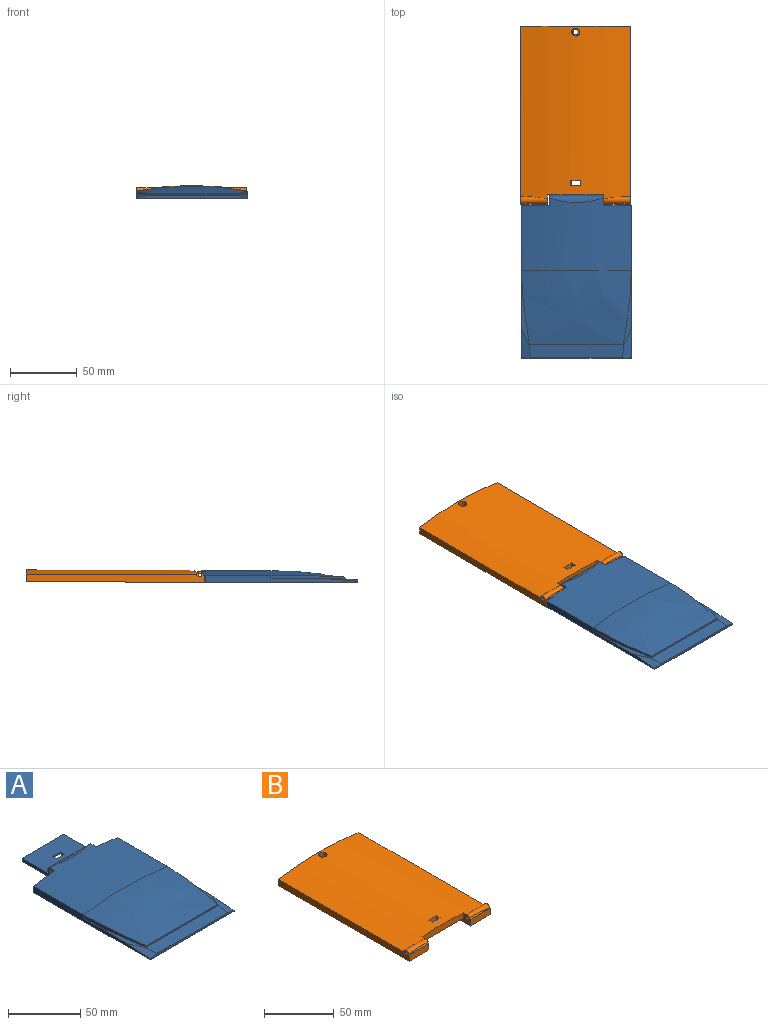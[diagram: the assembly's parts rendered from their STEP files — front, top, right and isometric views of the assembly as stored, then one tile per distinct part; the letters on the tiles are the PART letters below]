
ASSEMBLY  parts=2 mates=1
PART A: 33 faces, bbox 82x146x8.9 mm
  f0: plane 146x82mm, normal (0,0,-1), area 10463.6mm2, adj f2,f3,f7,f15,f16,f17,f18,f23
  f1: plane 40.8x2.7mm, normal (0,1,0), area 110.2mm2, adj f17,f18,f21,f22
  f2: plane 114x5.5mm, normal (1,0,0), area 419mm2, adj f0,f5,f6,f7,f9,f11,f15
  f3: plane 114x5.5mm, normal (-1,0,0), area 419mm2, adj f0,f4,f5,f7,f8,f13,f16
  f4: plane 55x6mm, normal (0,0,1), area 91mm2, adj f3,f8,f13,f14
  f5: cylinder r=250mm len=82mm, axis (0,1,0), area 4170mm2, adj f2,f3,f12,f15,f16,f17,f18,f20
  f6: plane 55x6mm, normal (0,0,1), area 91mm2, adj f2,f9,f11,f14
  f7: plane 82x2mm, normal (0,-1,0), area 156.3mm2, adj f0,f2,f3,f8,f9,f14
  f8: plane 22x6.61mm, normal (-0.17,-0.08,0.98), area 94.8mm2, adj f3,f4,f7,f14
  f9: plane 22x6.61mm, normal (0.17,-0.08,0.98), area 94.8mm2, adj f2,f6,f7,f14
  f10: plane 70x1.4mm, normal (0,-1,0), area 98mm2, adj f11,f12,f13,f14
  f11: bspline ~55x6mm, area 129.4mm2, adj f2,f6,f10,f12
  f12: bspline ~82x55mm, area 4285.9mm2, adj f5,f10,f11,f13
  f13: bspline ~55x6mm, area 129.4mm2, adj f3,f4,f10,f12
  f14: plane 71.09x10mm, normal (0,-0.06,1), area 700.6mm2, adj f4,f6,f7,f8,f9,f10
  f15: plane 20.6x8.05mm, normal (0,1,0), area 142.6mm2, adj f0,f2,f5,f17
  f16: plane 20.6x8.05mm, normal (0,1,0), area 142.6mm2, adj f0,f3,f5,f18
  f17: plane 32x8.05mm, normal (1,0,0), area 117.7mm2, adj f0,f1,f5,f15,f19,f21,f22,f23
  f18: plane 32x8.05mm, normal (-1,0,0), area 117.7mm2, adj f0,f1,f5,f16,f19,f21,f22,f23
  f19: cylinder r=1.25mm len=40.8mm, axis (1,0,0), area 320.4mm2, adj f17,f18
  f20: plane 33.11x2.62mm, normal (0,0.21,0.98), area 59mm2, adj f5,f21
  f21: cylinder r=3mm len=40.8mm, axis (1,0,0), area 163.7mm2, adj f1,f5,f17,f18,f20
  f22: plane 40.8x25mm, normal (0,0,1), area 988mm2, adj f1,f17,f18,f23,f29,f30,f31,f32
  f23: plane 40.8x2.7mm, normal (0,1,0), area 110.2mm2, adj f0,f17,f18,f22
  f24: plane 19x1.3mm, normal (0,-1,0), area 24.7mm2, adj f0,f25,f27,f28
  f25: plane 10x1.3mm, normal (-1,0,0), area 13mm2, adj f0,f24,f26,f28
  f26: plane 19x1.3mm, normal (0,1,0), area 24.7mm2, adj f0,f25,f27,f28
  f27: plane 10x1.3mm, normal (1,0,0), area 13mm2, adj f0,f24,f26,f28
  f28: plane 19x10mm, normal (0,0,-1), area 158mm2, adj f24,f25,f26,f27,f29,f30,f31,f32
  f29: plane 4x1.4mm, normal (-1,0,0), area 5.6mm2, adj f22,f28,f30,f32
  f30: plane 8x1.4mm, normal (0,1,0), area 11.2mm2, adj f22,f28,f29,f31
  f31: plane 4x1.4mm, normal (1,0,0), area 5.6mm2, adj f22,f28,f30,f32
  f32: plane 8x1.4mm, normal (0,-1,0), area 11.2mm2, adj f22,f28,f29,f31
PART B: 27 faces, bbox 82x133x8.9 mm
  f0: cylinder r=250mm len=8.18mm, axis (0,1,0), area 1.1mm2, adj f10,f12,f20
  f1: plane 33x8.05mm, normal (-1,0,0), area 140mm2, adj f7,f8,f11,f13,f16,f17,f19,f21
  f2: plane 6x6mm, normal (0,0,1), area 15.7mm2, adj f3,f5
  f3: cylinder r=3mm len=7.47mm, axis (0,0,-1), area 140.7mm2, adj f2,f11
  f4: plane 82x8.89mm, normal (0,1,0), area 636.3mm2, adj f7,f11,f12,f14
  f5: cylinder r=2mm len=4mm, axis (0,0,-1), area 17.6mm2, adj f2,f7
  f6: cylinder r=1.25mm len=20mm, axis (1,0,0), area 157.1mm2, adj f12,f15
  f7: plane 133x82mm, normal (0,0,-1), area 9507.4mm2, adj f1,f4,f5,f12,f14,f15,f17,f18
  f8: cylinder r=2.65mm len=20mm, axis (1,0,0), area 110mm2, adj f1,f9,f11,f14,f19
  f9: cylinder r=250mm len=8.18mm, axis (0,1,0), area 1.1mm2, adj f8,f14,f19
  f10: cylinder r=2.65mm len=20mm, axis (1,0,0), area 110mm2, adj f0,f11,f12,f15,f20
  f11: cylinder r=250mm len=129.49mm, axis (0,1,0), area 10399.8mm2, adj f1,f3,f4,f8,f10,f12,f14,f15
  f12: plane 133x8.05mm, normal (-1,0,0), area 737.1mm2, adj f0,f4,f6,f7,f10,f11,f18
  f13: cylinder r=1.25mm len=20mm, axis (1,0,0), area 157.1mm2, adj f1,f14
  f14: plane 133x8.05mm, normal (1,0,0), area 737.1mm2, adj f4,f7,f8,f9,f11,f13,f17
  f15: plane 33x8.05mm, normal (1,0,0), area 140mm2, adj f6,f7,f10,f11,f16,f18,f20,f21
  f16: plane 42x5.39mm, normal (0,-1,0), area 213.8mm2, adj f1,f11,f15,f21
  f17: plane 20x5.5mm, normal (0,-1,0), area 110mm2, adj f1,f7,f14,f19
  f18: plane 20x5.5mm, normal (0,-1,0), area 110mm2, adj f7,f12,f15,f20
  f19: plane 20.04x1.26mm, normal (0,-0.87,0.5), area 22.6mm2, adj f1,f8,f9,f17
  f20: plane 20.04x1.26mm, normal (0,-0.87,0.5), area 22.6mm2, adj f0,f10,f15,f18
  f21: plane 42x26mm, normal (0,0,-1), area 1060mm2, adj f1,f15,f16,f22,f23,f24,f25,f26
  f22: plane 42x3.5mm, normal (0,-1,0), area 147mm2, adj f1,f7,f15,f21
  f23: plane 5.35x4mm, normal (-1,0,0), area 21.4mm2, adj f11,f21,f24,f26
  f24: plane 8x5.39mm, normal (0,1,0), area 43mm2, adj f11,f21,f23,f25
  f25: plane 5.35x4mm, normal (1,0,0), area 21.4mm2, adj f11,f21,f24,f26
  f26: plane 8x5.39mm, normal (0,-1,0), area 43mm2, adj f11,f21,f23,f25
PLACE A t=(-101.88,43.36,-37.11)mm fixed
PLACE B rot(axis=(1,0,0),0.3deg) t=(-102.48,43.39,-36.44)mm
MATE revolute B.f6 <-> A.f19  axis (1,0,0) through (-81.48,-86.64,-31.71)mm
